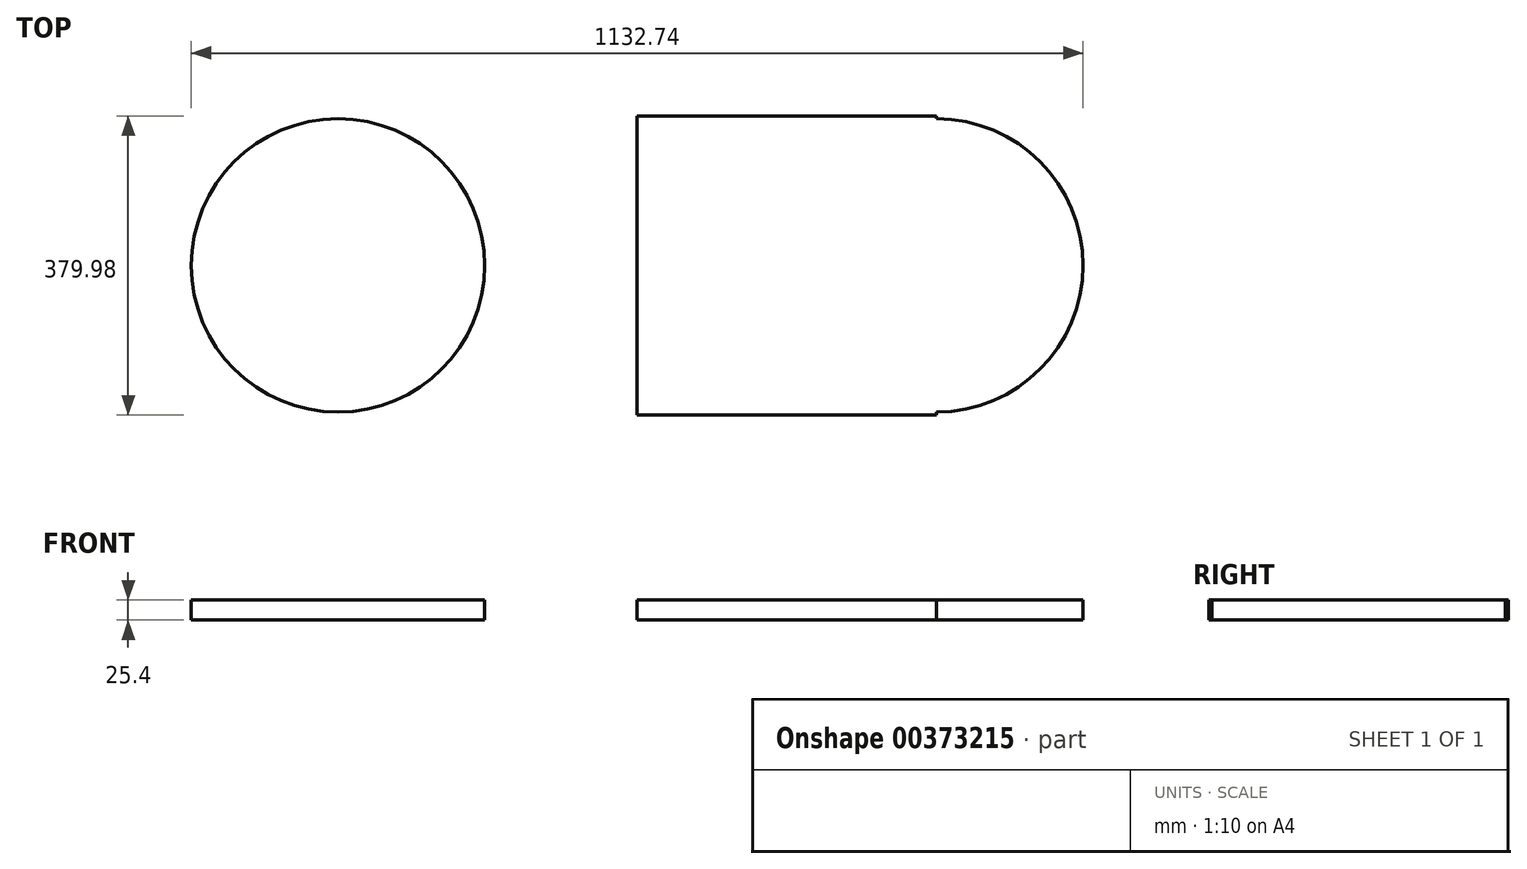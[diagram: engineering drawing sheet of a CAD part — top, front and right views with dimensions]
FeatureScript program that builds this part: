
annotation { "Feature Type Name" : "Feature", "Feature Type Description" : "" }
export const myFeature = defineFeature(function(context is Context, id is Id, definition is map)
    precondition{}
    {
        {
            var Q0;
            Q0=qCreatedBy(makeId("Top.planeOp"),FACE);
            var sketch = newSketch(context, id + "F0", { "sketchPlane" : qUnion([Q0])});
            skLineSegment(sketch, "E0.bottom", {"start": v(0, 0) * mm, "end": v(379.98, 0) * mm});
            skLineSegment(sketch, "E0.top", {"start": v(0, 379.98) * mm, "end": v(379.98, 379.98) * mm});
            skLineSegment(sketch, "E0.left", {"start": v(0, 0) * mm, "end": v(0, 379.98) * mm});
            skLineSegment(sketch, "E0.right", {"start": v(379.98, 0) * mm, "end": v(379.98, 379.98) * mm});
            skCircle(sketch, "E1", {"center": v(379.98, 190) * mm, "radius": 186.4 * mm});
            skCircle(sketch, "E2.MirrorC", {"center": v(-379.98, 190) * mm, "radius": 186.4 * mm});
            skLineSegment(sketch, "E3.MirrorCS", {"start": v(0, 379.98) * mm, "end": v(-379.98, 379.98) * mm});
            skLineSegment(sketch, "E4.MirrorCS", {"start": v(0, 0) * mm, "end": v(-379.98, 0) * mm});
            skSolve(sketch);
        }
        {
            var Q0;
            Q0 = qSketchRegion(id + "F0", true);
            extrude(context, id + "F1", {"entities" : qUnion([Q0]), "depth" : 25.4 * mm});
        }
    });
